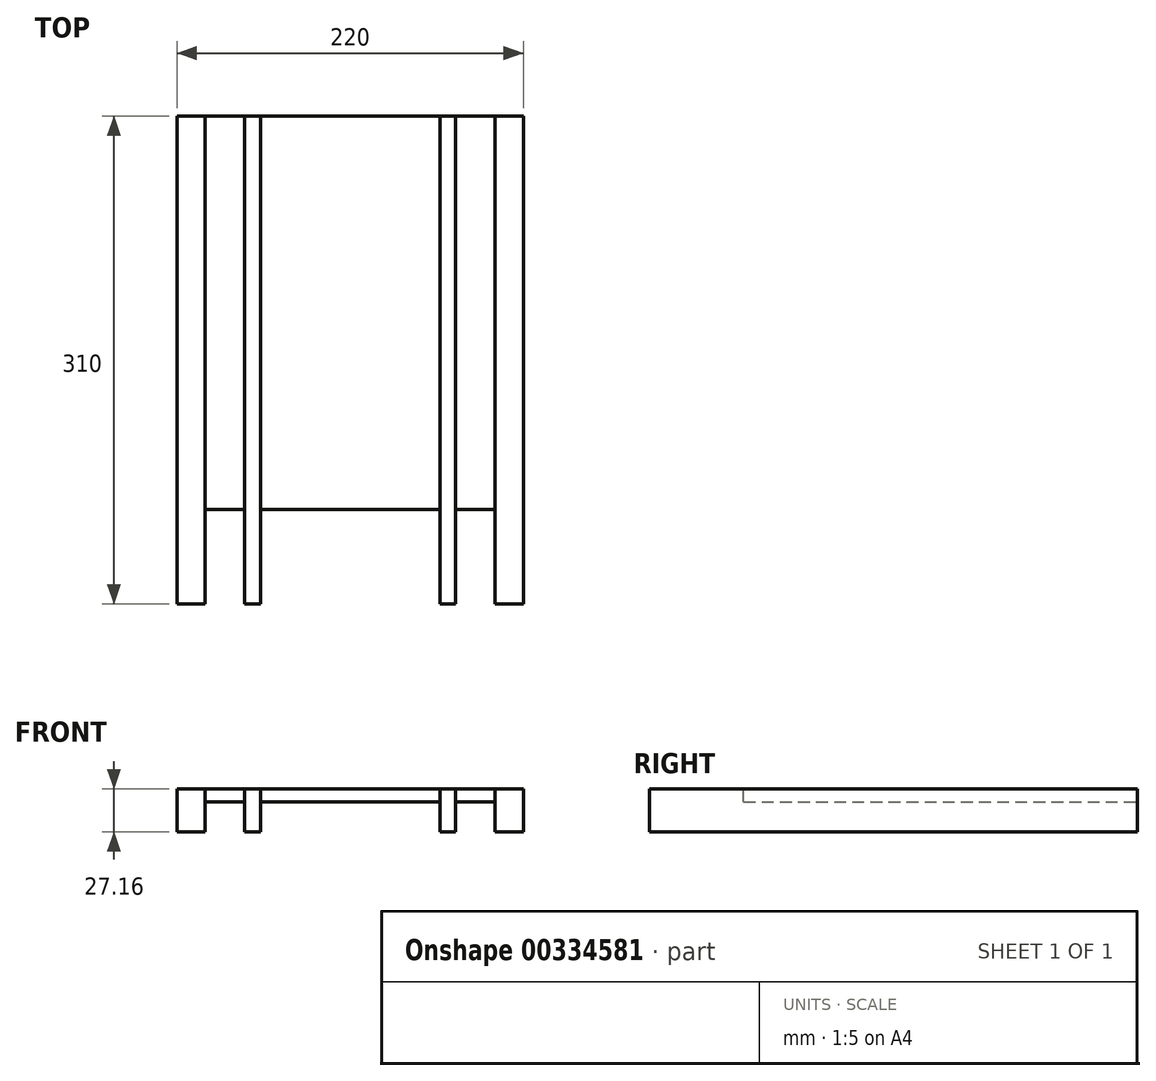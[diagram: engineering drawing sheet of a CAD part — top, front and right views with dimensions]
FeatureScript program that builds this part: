
annotation { "Feature Type Name" : "Feature", "Feature Type Description" : "" }
export const myFeature = defineFeature(function(context is Context, id is Id, definition is map)
    precondition{}
    {
        {
            var Q0;
            Q0=qCreatedBy(makeId("Front.planeOp"),FACE);
            var sketch = newSketch(context, id + "F0", { "sketchPlane" : qUnion([Q0])});
            skLineSegment(sketch, "E0.top", {"start": v(-51.02, -19.16) * mm, "end": v(-69.02, -19.16) * mm});
            skLineSegment(sketch, "E0.left", {"start": v(-51.02, 0) * mm, "end": v(-51.02, -19.16) * mm});
            skLineSegment(sketch, "E0.right", {"start": v(-69.02, 3.84) * mm, "end": v(-69.02, -19.16) * mm});
            skLineSegment(sketch, "E1.top", {"start": v(132.98, -19.16) * mm, "end": v(150.98, -19.16) * mm});
            skLineSegment(sketch, "E1.left", {"start": v(132.98, 0) * mm, "end": v(132.98, -19.16) * mm});
            skLineSegment(sketch, "E1.right", {"start": v(150.98, 3.84) * mm, "end": v(150.98, -19.16) * mm});
            skLineSegment(sketch, "E2.bottom", {"start": v(97.98, 0) * mm, "end": v(-16.02, 0) * mm});
            skLineSegment(sketch, "E3.top", {"start": v(-69.02, 8) * mm, "end": v(150.98, 8) * mm});
            skLineSegment(sketch, "E3.left", {"start": v(-69.02, 3.84) * mm, "end": v(-69.02, 8) * mm});
            skLineSegment(sketch, "E3.right", {"start": v(150.98, 3.84) * mm, "end": v(150.98, 8) * mm});
            skLineSegment(sketch, "E4.0", {"start": v(-26.02, 0) * mm, "end": v(-26.02, -19.16) * mm});
            skLineSegment(sketch, "E5.0", {"start": v(107.98, 0) * mm, "end": v(107.98, -19.16) * mm});
            skLineSegment(sketch, "E6.0", {"start": v(-16.02, 0) * mm, "end": v(-16.02, -19.16) * mm});
            skLineSegment(sketch, "E7.0", {"start": v(97.98, 0) * mm, "end": v(97.98, -19.16) * mm});
            skLineSegment(sketch, "E8", {"start": v(-16.02, -19.16) * mm, "end": v(-26.02, -19.16) * mm});
            skLineSegment(sketch, "E9", {"start": v(97.98, -19.16) * mm, "end": v(107.98, -19.16) * mm});
            skLineSegment(sketch, "E10", {"start": v(132.98, 0) * mm, "end": v(107.98, 0) * mm});
            skLineSegment(sketch, "E11", {"start": v(-51.02, 0) * mm, "end": v(-26.02, 0) * mm});
            skLineSegment(sketch, "E12", {"start": v(-51.02, 0) * mm, "end": v(-51.02, 8) * mm});
            skLineSegment(sketch, "E13", {"start": v(132.98, 0) * mm, "end": v(132.98, 8) * mm});
            skLineSegment(sketch, "E14", {"start": v(-26.02, 0) * mm, "end": v(-26.02, 8) * mm});
            skLineSegment(sketch, "E15", {"start": v(-16.02, 0) * mm, "end": v(-16.02, 8) * mm});
            skLineSegment(sketch, "E16", {"start": v(97.98, 0) * mm, "end": v(97.98, 8) * mm});
            skLineSegment(sketch, "E17", {"start": v(107.98, 0) * mm, "end": v(107.98, 8) * mm});
            skSolve(sketch);
        }
        {
            var Q0;
            Q0=makeQuery(id+"F0.imprint","IMPRINT",FACE,{"disambiguationData":[TD([[makeQuery(id+"F0.imprint","IMPRINT",EDGE,{"derivedFrom":sQuery(id+"F0.wireOp",EDGE,"E1.top")}),1.0]])]});
            var Q1;
            Q1=makeQuery(id+"F0.imprint","IMPRINT",FACE,{"disambiguationData":[TD([[makeQuery(id+"F0.imprint","IMPRINT",EDGE,{"derivedFrom":sQuery(id+"F0.wireOp",EDGE,"E0.top")}),-1.0]])]});
            extrude(context, id + "F1", {"entities" : qUnion([Q0, Q1]), "depth" : 310 * mm});
        }
        {
            var Q0;
            Q0=makeQuery(id+"F0.imprint","IMPRINT",FACE,{"disambiguationData":[TD([[makeQuery(id+"F0.imprint","IMPRINT",EDGE,{"derivedFrom":sQuery(id+"F0.wireOp",EDGE,"E2.bottom")}),-1.0]])]});
            extrude(context, id + "F2", {"entities" : qUnion([Q0]), "depth" : 250 * mm});
        }
        {
            var Q0;
            Q0=makeQuery(id+"F0.imprint","IMPRINT",FACE,{"disambiguationData":[TD([[makeQuery(id+"F0.imprint","IMPRINT",EDGE,{"derivedFrom":sQuery(id+"F0.wireOp",EDGE,"E4.0")}),1.0]])]});
            var Q1;
            Q1=makeQuery(id+"F0.imprint","IMPRINT",FACE,{"disambiguationData":[TD([[makeQuery(id+"F0.imprint","IMPRINT",EDGE,{"derivedFrom":sQuery(id+"F0.wireOp",EDGE,"E5.0")}),-1.0]])]});
            extrude(context, id + "F3", {"entities" : qUnion([Q0, Q1]), "operationType" : NewBodyOperationType.ADD, "depth" : 310 * mm});
        }
        {
            var Q0;
            Q0=makeQuery(id+"F0.imprint","IMPRINT",FACE,{"disambiguationData":[TD([[makeQuery(id+"F0.imprint","IMPRINT",EDGE,{"derivedFrom":sQuery(id+"F0.wireOp",EDGE,"E11")}),1.0]])]});
            var Q1;
            Q1=makeQuery(id+"F0.imprint","IMPRINT",FACE,{"disambiguationData":[TD([[makeQuery(id+"F0.imprint","IMPRINT",EDGE,{"derivedFrom":sQuery(id+"F0.wireOp",EDGE,"E10")}),-1.0]])]});
            var Q2;
            Q2=makeQuery(id+"F0.imprint","IMPRINT",FACE,{"disambiguationData":[TD([[makeQuery(id+"F0.imprint","IMPRINT",EDGE,{"derivedFrom":sQuery(id+"F0.wireOp",EDGE,"E2.bottom")}),-1.0]])]});
            extrude(context, id + "F4", {"entities" : qUnion([Q0, Q1, Q2]), "depth" : 250 * mm});
        }
    });
